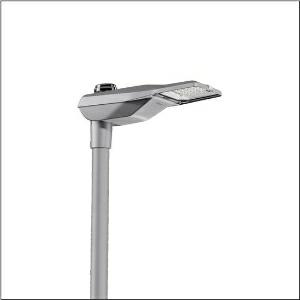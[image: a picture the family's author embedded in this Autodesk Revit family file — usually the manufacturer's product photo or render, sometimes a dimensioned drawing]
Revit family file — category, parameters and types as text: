
# Revit family: streetlight_sl_21_micro___p0_8a_5xe5u47n08db_d803
name_source: partatom
category: Lighting Fixtures
units: mm (PartAtom-declared; Revit-internal decimal feet)

## family parameters
Cut with Voids When Loaded = No
Host = Face
Light Source = No
Part Type = Normal
Room Calculation Point = No
Round Connector Dimension = Use Diameter
Shared = No

## types (1)
- --- (1 x LED, 5250 lm, 39.1 W, 4000K)
    Apparent Load = 39 VA
    CIE Flux Codes = 33 69 96 100 100
    Color Rendering = 70
    Color Temperature = 4000K
    Default Elevation = 1800 mm
    Description = Streetlight SL 21 micro, mast luminaire, primary light control with lens, of PMMA, primary optical cover: cover, of toughened safety glass, transparent, light distribution: P0.8a, light emission: direct distribution, primary light characteristic: asymmetric, installation type: post-top, LED, 3G 1.5mm², High Power LED, rated luminous flux: 5.250lm, luminous efficacy: 134lm/W, light colour: 740, colour temperature: 4000K, control gear: NEMA (7pin), control: flexible luminous flux parameterisation, time-dependent luminous flux control, constant luminous flux control, pre-setting: linear dimming characteristic, overheat protection, mains connection: 230..240V, AC, 50/60Hz, connection cable pre-assembled, cable length: 6,5m, wiring characteristics: H07RN-F, start of lifetime: 39W, end of service life: 41W, reduction: 18W, luminaire housing, of diecast aluminium (EN AC-44300), powder-coated, Siteco® metallic grey (DB 702S), corrosivity category C5 mid according to DIN EN ISO 12944, multi-level sealing system, sealing non-destructively replaceable, inclination adjustable: 0°, 5°, 10°, 15°, length: 528mm, width: 235mm, height: 110mm, spigot size: 76/60mm (post-top), mounting height: 4..8m, protection rating (complete): IP66, insulation class (complete): insulation class I (protective earthing), certification: CE, ENEC, ENEC+, VDE, impact resistance: IK10, permissible operating ambient temperature for outdoor applications: -40..+50°C, standard-compliant lighting for roads and squares, packaging unit: 1 piece

Light Distribution: P0.8a
    Height = 110 mm
    Lamp = 1 x LED
    Lamp Light Flux = 5250 lm
    Lamp Power = 39.1 W
    Lamp count = 1
    Length = 528 mm
    Luminous efficacy = 134 lm/W
    Manufacturer = Siteco
    ModVariant = No
    Model = 5XE5U47N08DB
    Number of Poles = 1
    OnlyDefault = Yes
    Power Factor = 1
    Product Name = Streetlight SL 21 micro | P0.8a
    Product group = mast luminaire | pylon top
    ProductGroupID = 6100
    Protection Class = Protection class I
    Protection Degree = IP 66
    RLX_Detail_Level = 1
    RLX_Emergency_Light_Flux = 0 lm
    RLX_Emergency_Type = 0
    RLX_Emergency_Type_DB = No
    RlxData = <blob elided: 98413 chars, md5=531b5d3f>
    Socket = socket
    Standby Power = 0 W
    System Light Flux = 5250 lm
    System Power = 39 W
    Type Comments = factory setting: luminous flux: 100 % | dim-lin: 254 | 765 mA
    Type Image = l_1294375.jpg
    URL = http://relux.com
    VarID = @adj_095291
    Voltage = 0 V
    Weight = 0.00 kg
    Width = 235 mm

## geometry (parser evidence)
native form markers: Blend x4, Sweep x10
no freeform markers — native parametric forms only
